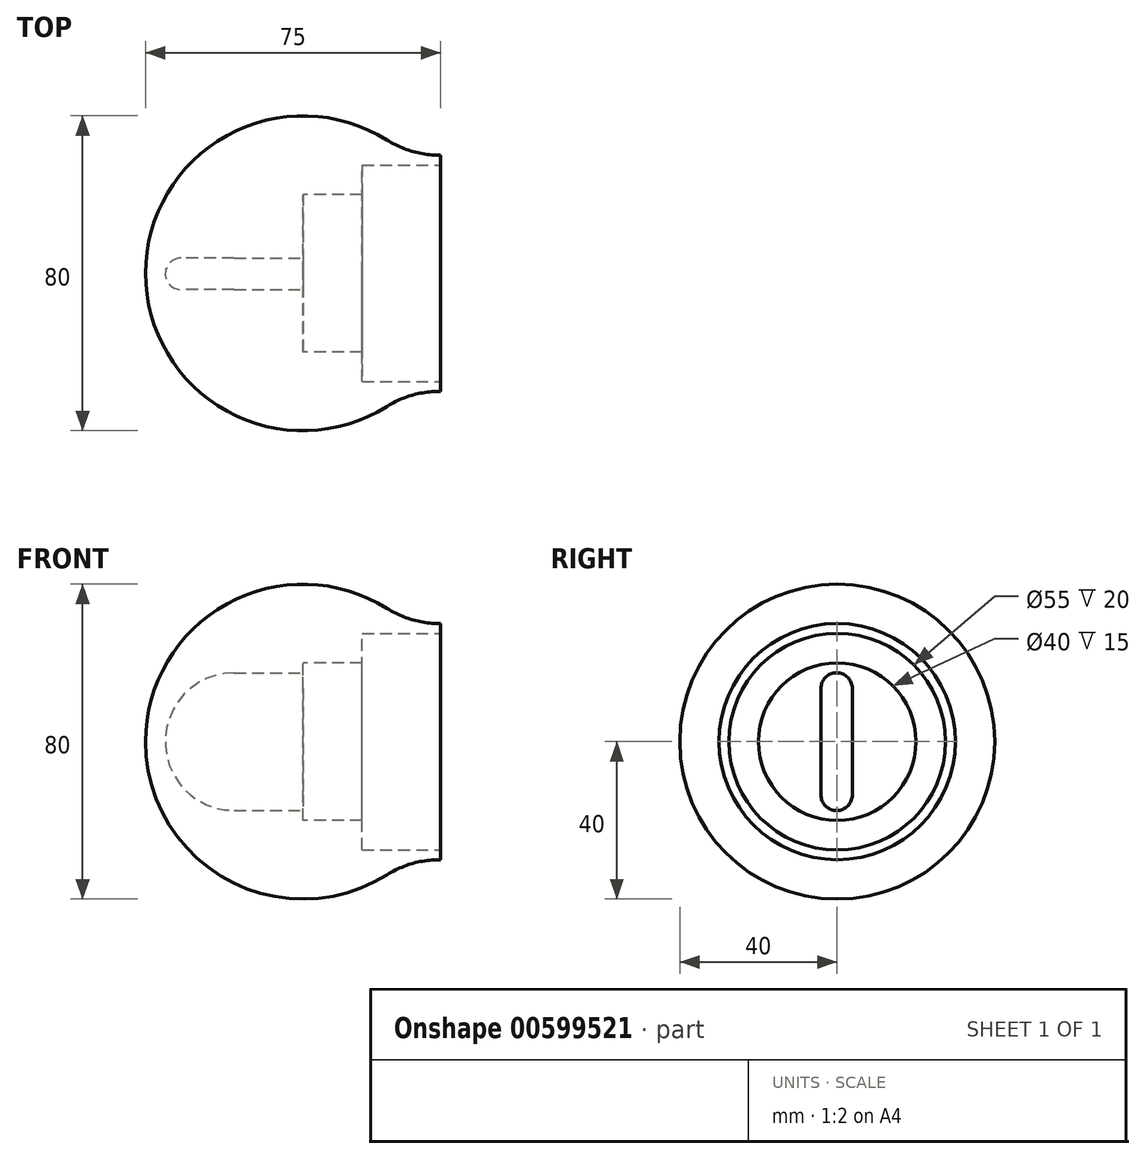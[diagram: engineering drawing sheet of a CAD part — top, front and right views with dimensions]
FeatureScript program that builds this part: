
annotation { "Feature Type Name" : "Feature", "Feature Type Description" : "" }
export const myFeature = defineFeature(function(context is Context, id is Id, definition is map)
    precondition{}
    {
        {
            var Q0;
            Q0=qCreatedBy(makeId("Front.planeOp"),FACE);
            var sketch = newSketch(context, id + "F0", { "sketchPlane" : qUnion([Q0])});
            skLineSegment(sketch, "E0", {"start": v(-40, 0) * mm, "end": v(40, 0) * mm});
            skArc(sketch, "E1", {"start": v(-40, 0) * mm, "mid": v(0, 40) * mm, "end": v(40, 0) * mm});
            skSolve(sketch);
        }
        {
            var Q0;
            Q0=makeQuery(id+"F0.imprint","IMPRINT",FACE,{"disambiguationData":[TD([[makeQuery(id+"F0.imprint","IMPRINT",EDGE,{"derivedFrom":sQuery(id+"F0.wireOp",EDGE,"E0")}),1.0]])]});
            var Q1;
            Q1=sQuery(id+"F0.wireOp",EDGE,"E0");
            revolve(context, id + "F1", {"entities" : qUnion([Q0]), "axis" : qUnion([Q1]), "revolveType" : RevolveType.FULL});
        }
        {
            var Q0;
            Q0=qCreatedBy(makeId("Right.planeOp"),FACE);
            var sketch = newSketch(context, id + "F2", { "sketchPlane" : qUnion([Q0])});
            skCircle(sketch, "E2", {"center": v(0, 0) * mm, "radius": 20 * mm});
            skSolve(sketch);
        }
        {
            var Q0;
            Q0 = qSketchRegion(id + "F2", true);
            extrude(context, id + "F3", {"entities" : qUnion([Q0]), "operationType" : NewBodyOperationType.REMOVE, "depth" : 61.6 * mm, "offsetDistance" : 25 * mm});
        }
        {
            var Q0;
            Q0=makeQuery(id+"F3.boolean.opBoolean","COPY",FACE,{"derivedFrom":makeQuery(id+"F3.opExtrude","CAP_FACE",FACE,{"disambiguationData":[OSD([sQuery(id+"F2.wireOp",EDGE,"E2"),sQuery(id+"F2.wireOp",EDGE,"272fddd2-ee6c-4783-b963-abafeb4d9a85.filletArc"),sQuery(id+"F2.wireOp",EDGE,"7f18eaed-ad29-4d42-956e-3c9b3a1bd9ab.filletArc"),sQuery(id+"F2.wireOp",EDGE,"d35aef29-00ff-4858-9d55-779e7f0ff2e5.filletArc"),sQuery(id+"F2.wireOp",EDGE,"04580f28-3515-4f07-bfd4-56c0b641af99.filletArc")])],"isStart":true})});
            var sketch = newSketch(context, id + "F4", { "sketchPlane" : qUnion([Q0])});
            skSolve(sketch);
        }
        {
            var Q0;
            Q0=qCreatedBy(makeId("Right.planeOp"),FACE);
            var sketch = newSketch(context, id + "F5", { "sketchPlane" : qUnion([Q0])});
            skCircle(sketch, "E3", {"center": v(0, 0) * mm, "radius": 20 * mm});
            skCircle(sketch, "E4", {"center": v(0, 0) * mm, "radius": 30 * mm});
            skSolve(sketch);
        }
        {
            var Q0;
            Q0 = qSketchRegion(id + "F5", true);
            extrude(context, id + "F6", {"entities" : qUnion([Q0]), "operationType" : NewBodyOperationType.ADD, "depth" : 35 * mm, "offsetDistance" : 25 * mm});
        }
        {
            var Q0;
            Q0=makeQuery(id+"F6.opExtrude","CAP_FACE",FACE,{"disambiguationData":[OSD([sQuery(id+"F5.wireOp",EDGE,"E3"),sQuery(id+"F5.wireOp",EDGE,"E4")])],"isStart":false});
            var sketch = newSketch(context, id + "F7", { "sketchPlane" : qUnion([Q0])});
            skCircle(sketch, "E5", {"center": v(0, 0) * mm, "radius": 27.5 * mm});
            skCircle(sketch, "E6", {"center": v(0, 0) * mm, "radius": 20 * mm});
            skSolve(sketch);
        }
        {
            var Q0;
            Q0 = qSketchRegion(id + "F7", true);
            extrude(context, id + "F8", {"entities" : qUnion([Q0]), "operationType" : NewBodyOperationType.REMOVE, "oppositeDirection" : true, "depth" : 20 * mm, "offsetDistance" : 25 * mm});
        }
        {
            var Q0;
            Q0=makeQuery(id+"F6.boolean.opBoolean","INTERSECT",EDGE,{"derivedFrom":[makeQuery(id+"F1.opRevolve","SWEPT_FACE",FACE,{"disambiguationData":[OSD([sQuery(id+"F0.wireOp",EDGE,"E1")])]}),makeQuery(id+"F6.opExtrude","SWEPT_FACE",FACE,{"disambiguationData":[OSD([sQuery(id+"F5.wireOp",EDGE,"E4")])]})]});
            fillet(context, id + "F9", {"entities" : qUnion([Q0]), "radius" : 25 * mm, "tangentPropagation" : true, "allowEdgeOverflow" : false});
        }
        {
            var Q0;
            Q0=makeQuery(id+"F4.imprint","IMPRINT",FACE,{"disambiguationData":[TD([[makeQuery(id+"F4.imprint","IMPRINT",EDGE,{"derivedFrom":makeQuery(id+"F3.boolean.opBoolean","COPY",EDGE,{"derivedFrom":makeQuery(id+"F3.opExtrude","CAP_EDGE",EDGE,{"disambiguationData":[OSD([sQuery(id+"F2.wireOp",EDGE,"E2")])],"isStart":true})})}),1.0]])]});
            var sketch = newSketch(context, id + "F10", { "sketchPlane" : qUnion([Q0])});
            skLineSegment(sketch, "E7", {"start": v(-4.15, 13.5) * mm, "end": v(3.85, 13.5) * mm});
            skArc(sketch, "E8", {"start": v(3.85, 13.5) * mm, "mid": v(-0.15, 17.5) * mm, "end": v(-4.15, 13.5) * mm});
            skLineSegment(sketch, "E9", {"start": v(3.85, 13.5) * mm, "end": v(3.85, 0) * mm});
            skLineSegment(sketch, "E10", {"start": v(3.85, 0) * mm, "end": v(-4.15, 0) * mm});
            skLineSegment(sketch, "E11", {"start": v(-4.15, 0) * mm, "end": v(-4.15, 13.5) * mm});
            skLineSegment(sketch, "E12.MirrorCS", {"start": v(-4.15, 0) * mm, "end": v(-4.15, -13.5) * mm});
            skLineSegment(sketch, "E13.MirrorCS", {"start": v(3.85, -13.5) * mm, "end": v(3.85, 0) * mm});
            skArc(sketch, "E14.MirrorCS", {"start": v(3.85, -13.5) * mm, "mid": v(-0.15, -17.5) * mm, "end": v(-4.15, -13.5) * mm});
            skLineSegment(sketch, "E15.MirrorCS", {"start": v(-4.15, -13.5) * mm, "end": v(3.85, -13.5) * mm});
            skSolve(sketch);
        }
        {
            var Q0;
            Q0 = qSketchRegion(id + "F10", true);
            extrude(context, id + "F11", {"entities" : qUnion([Q0]), "operationType" : NewBodyOperationType.REMOVE, "oppositeDirection" : true, "depth" : 17.5 * mm, "offsetDistance" : 25 * mm});
        }
        {
            var Q0;
            Q0=makeQuery(id+"F11.boolean.opBoolean","COPY",FACE,{"derivedFrom":makeQuery(id+"F11.opExtrude","CAP_FACE",FACE,{"disambiguationData":[OSD([sQuery(id+"F10.wireOp",EDGE,"E8"),sQuery(id+"F10.wireOp",EDGE,"E9"),sQuery(id+"F10.wireOp",EDGE,"E11"),sQuery(id+"F10.wireOp",EDGE,"E12.MirrorCS"),sQuery(id+"F10.wireOp",EDGE,"E13.MirrorCS"),sQuery(id+"F10.wireOp",EDGE,"E14.MirrorCS")])],"isStart":false})});
            var sketch = newSketch(context, id + "F12", { "sketchPlane" : qUnion([Q0])});
            skLineSegment(sketch, "E16", {"start": v(-4.15, 13.5) * mm, "end": v(3.85, 13.5) * mm});
            skArc(sketch, "E17", {"start": v(3.85, 13.5) * mm, "mid": v(-0.15, 17.5) * mm, "end": v(-4.15, 13.5) * mm});
            skLineSegment(sketch, "E18", {"start": v(3.85, 13.5) * mm, "end": v(3.85, 0) * mm});
            skLineSegment(sketch, "E19", {"start": v(3.85, 0) * mm, "end": v(-4.15, 0) * mm});
            skLineSegment(sketch, "E20", {"start": v(-4.15, 0) * mm, "end": v(-4.15, 13.5) * mm});
            skSolve(sketch);
        }
        {
            var Q0;
            Q0 = qSketchRegion(id + "F12", true);
            var Q1;
            Q1=sQuery(id+"F12.wireOp",EDGE,"E19");
            revolve(context, id + "F13", {"operationType" : NewBodyOperationType.REMOVE, "entities" : qUnion([Q0]), "axis" : qUnion([Q1]), "revolveType" : RevolveType.FULL, "oppositeDirection" : true});
        }
    });
